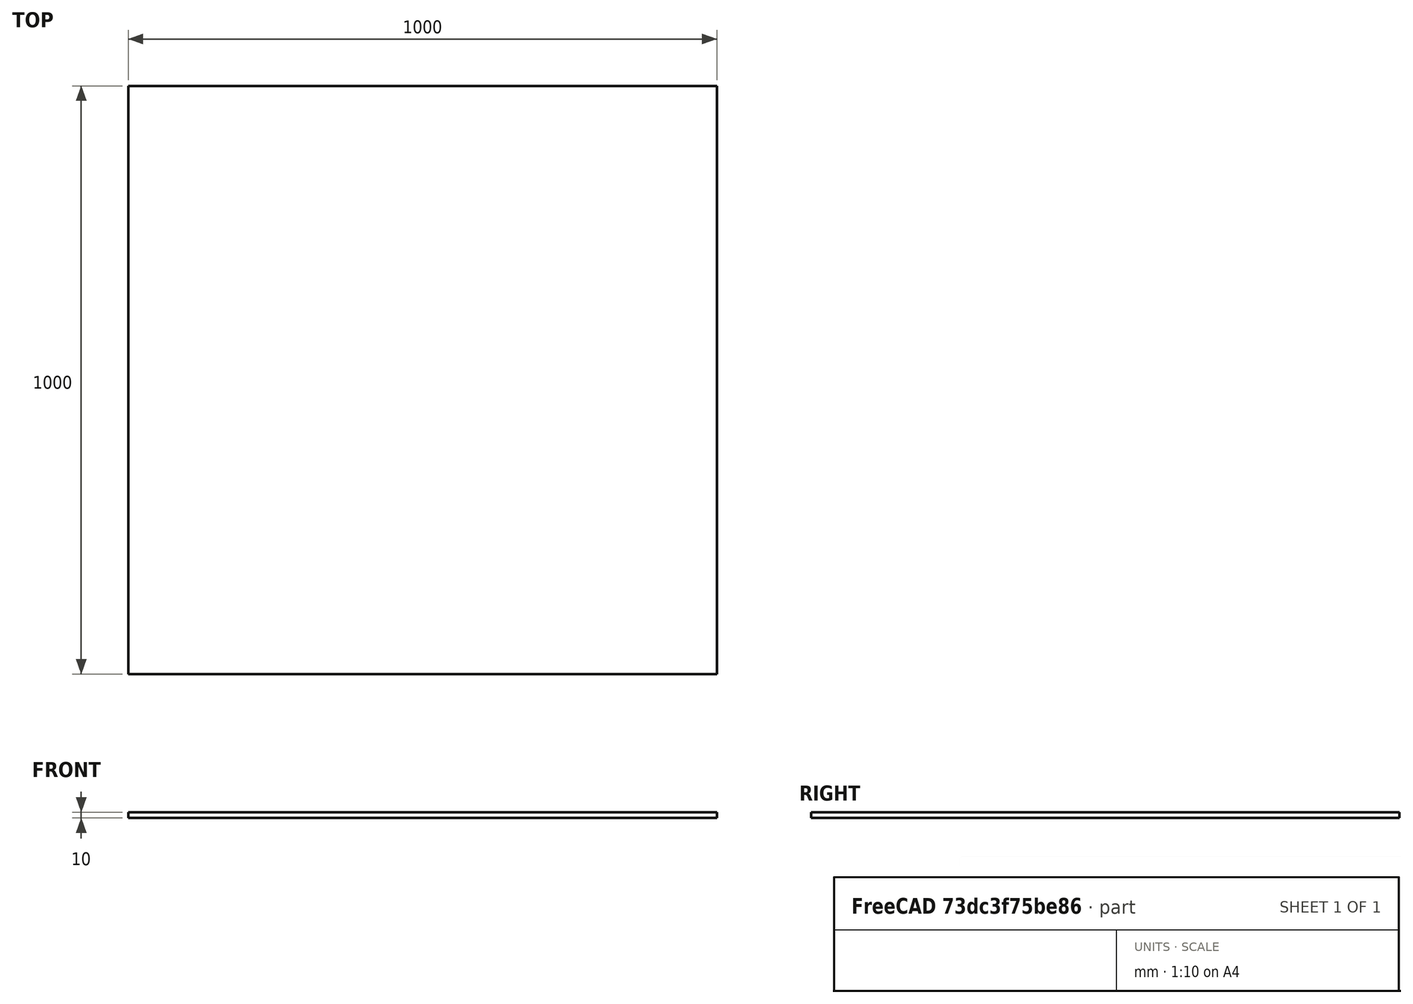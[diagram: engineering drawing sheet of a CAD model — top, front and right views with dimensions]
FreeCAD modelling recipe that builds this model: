
FCSTD DOCUMENT  (FreeCAD 0.21R33694 (Git))
Label: shear_panel
License: All rights reserved
LicenseURL: http://en.wikipedia.org/wiki/All_rights_reserved
objects: Fem::ConstraintForce×4, Fem::ConstraintDisplacement×2, Part::Box×1, App::MaterialObjectPython×1, Fem::FemSolverObjectPython×1, Fem::ConstraintFixed×1, Fem::FemMeshObjectPython×1, Fem::FemAnalysis×1
note: 1 computed .brp shape members not serialized (recipe doc carries the construction recipe); baked Part::Feature solids carry a one-line shape summary decoded from their .brp

FEATURE [Part::Box] Box  label="Cube"
  AttacherType = Attacher::AttachEngine3D
  Height = 10
  Length = 1000
  Width = 1000
FEATURE [Fem::ConstraintDisplacement] ConstraintDisplacement
  NormalDirection = (0,0,1)
  Normals = (16) [(0,0,1),(0,0,1),(0,0,1),(0,0,1),(0,0,1),(0,0,1),(0,0,1),(0,0,1),(0,0,1),(0,0,1),(0,0,1),(0,0,1),(0,0,1),(0,0,1),(0,0,1),(0,0,1)]
  Points = (16) [(0,0,0),(333.333,0,0),(666.667,0,0),(1000,0,0),(0,0,0),(0,333.333,0),(0,666.667,0),(0,1000,0),(1000,0,0),(1000,333.333,0),(1000,666.667,0),+5 more]
  References = -> [Box]
  Scale = 33
  hasXFormula = false
  hasYFormula = false
  hasZFormula = false
  rotxFix = false
  rotxFree = true
  rotyFix = false
  rotyFree = true
  rotzFix = false
  rotzFree = true
  useFlowSurfaceForce = false
  xDisplacement = 0
  xFix = false
  xFree = true
  xRotation = 0
  yDisplacement = 0
  yFix = false
  yFree = true
  yRotation = 0
  zDisplacement = 0
  zFix = false
  zFree = false
  zRotation = 0
FEATURE [Fem::ConstraintForce] ConstraintForce
  Direction = -> Box [Edge12]
  DirectionVector = (1,0,0)
  Force = 1000000
  NormalDirection = (0,1,0)
  Points = (15) [(0,1000,0),(0,1000,5),(0,1000,10),(250,1000,0),(250,1000,5),(250,1000,10),(500,1000,0),(500,1000,5),(500,1000,10),(750,1000,0),(750,1000,5),+4 more]
  References = -> [Box]
FEATURE [Fem::ConstraintForce] ConstraintForce001
  Direction = -> Box [Edge10]
  DirectionVector = (-1,0,0)
  Force = 1000000
  NormalDirection = (0,-1,0)
  Points = (15) [(0,0,0),(0,0,5),(0,0,10),(250,0,0),(250,0,5),(250,0,10),(500,0,0),(500,0,5),(500,0,10),(750,0,0),(750,0,5),(750,0,10),(1000,0,0),(1000,0,5),+1 more]
  References = -> [Box]
  Reversed = true
FEATURE [Fem::ConstraintForce] ConstraintForce002
  Direction = -> Box [Edge6]
  DirectionVector = (0,1,0)
  Force = 1000000
  NormalDirection = (1,0,0)
  Points = (15) [(1000,1000,0),(1000,1000,5),(1000,1000,10),(1000,750,0),(1000,750,5),(1000,750,10),(1000,500,0),(1000,500,5),(1000,500,10),(1000,250,0),(1000,250,5),+4 more]
  References = -> [Box]
FEATURE [Fem::ConstraintForce] ConstraintForce003
  Direction = -> Box [Edge2]
  DirectionVector = (0,-1,0)
  Force = 1000000
  NormalDirection = (-1,0,0)
  Points = (15) [(0,1000,0),(0,1000,5),(0,1000,10),(0,750,0),(0,750,5),(0,750,10),(0,500,0),(0,500,5),(0,500,10),(0,250,0),(0,250,5),(0,250,10),(0,0,0),(0,0,5),+1 more]
  References = -> [Box]
  Reversed = true
FEATURE [App::MaterialObjectPython] MaterialSolid  # material (typed FeaturePython)
  Category = 0
  Material = AuthorAndLicense=(c) 2014 M. Münch - GNU Lesser General Public License (LGPL),CardName=Steel-St-E-315,Density=7800 kg/m^3,Father=Metal,+13 more (map truncated)
FEATURE [Fem::FemSolverObjectPython] SolverCcxTools  # FEM object (typed FeaturePython)
  AnalysisType = 0
  BeamShellResultOutput3D = false
  BucklingFactors = 1
  EigenmodeHighLimit = 1000000
  EigenmodeLowLimit = 0
  EigenmodesCount = 10
  GeometricalNonlinearity = 0
  IterationsControlParameterCutb = 0.25,0.5,0.75,0.85,,,1.5,
  IterationsControlParameterIter = 4,8,9,200,10,400,,200,,
  IterationsControlParameterTimeUse = false
  IterationsThermoMechMaximum = 2000
  IterationsUserDefinedIncrementations = false
  IterationsUserDefinedTimeStepLength = false
  MaterialNonlinearity = 0
  MatrixSolverType = 0
  SplitInputWriter = false
  ThermoMechSteadyState = true
  TimeEnd = 1
  TimeInitialStep = 0.01
FEATURE [Fem::ConstraintFixed] ConstraintFixed
  NormalDirection = (0,0,1)
  Normals = (2) [(0,0,1),(0,0,1)]
  Points = (2) [(1000,1000,0),(1000,1000,10)]
  References = -> [Box]
FEATURE [Fem::ConstraintDisplacement] ConstraintDisplacement001
  NormalDirection = (0,0,1)
  Normals = (2) [(0,0,1),(0,0,1)]
  Points = (2) [(1000,0,0),(1000,0,10)]
  References = -> [Box]
  hasXFormula = false
  hasYFormula = false
  hasZFormula = false
  rotxFix = false
  rotxFree = true
  rotyFix = false
  rotyFree = true
  rotzFix = false
  rotzFree = true
  useFlowSurfaceForce = false
  xDisplacement = 0
  xFix = false
  xFree = false
  xRotation = 0
  yDisplacement = 0
  yFix = false
  yFree = true
  yRotation = 0
  zDisplacement = 0
  zFix = false
  zFree = true
  zRotation = 0
FEATURE [Fem::FemMeshObjectPython] FEMMeshGmsh  # FEM object (typed FeaturePython)
  Algorithm2D = 0
  Algorithm3D = 0
  CharacteristicLengthMax = 50
  CharacteristicLengthMin = 0
  CoherenceMesh = true
  ElementDimension = 0
  ElementOrder = 1
  GeometryTolerance = 1e-06
  GroupsOfNodes = false
  HighOrderOptimize = 0
  MeshSizeFromCurvature = 12
  OptimizeNetgen = false
  OptimizeStd = true
  Part = -> Box
  RecombinationAlgorithm = 0
  Recombine3DAll = false
  RecombineAll = false
  SecondOrderLinear = false
FEATURE [Fem::FemAnalysis] Analysis
  Group = -> [ConstraintDisplacement,ConstraintForce,ConstraintForce001,ConstraintForce002,ConstraintForce003,MaterialSolid,SolverCcxTools,ConstraintFixed,ConstraintDisplacement001,FEMMeshGmsh]
